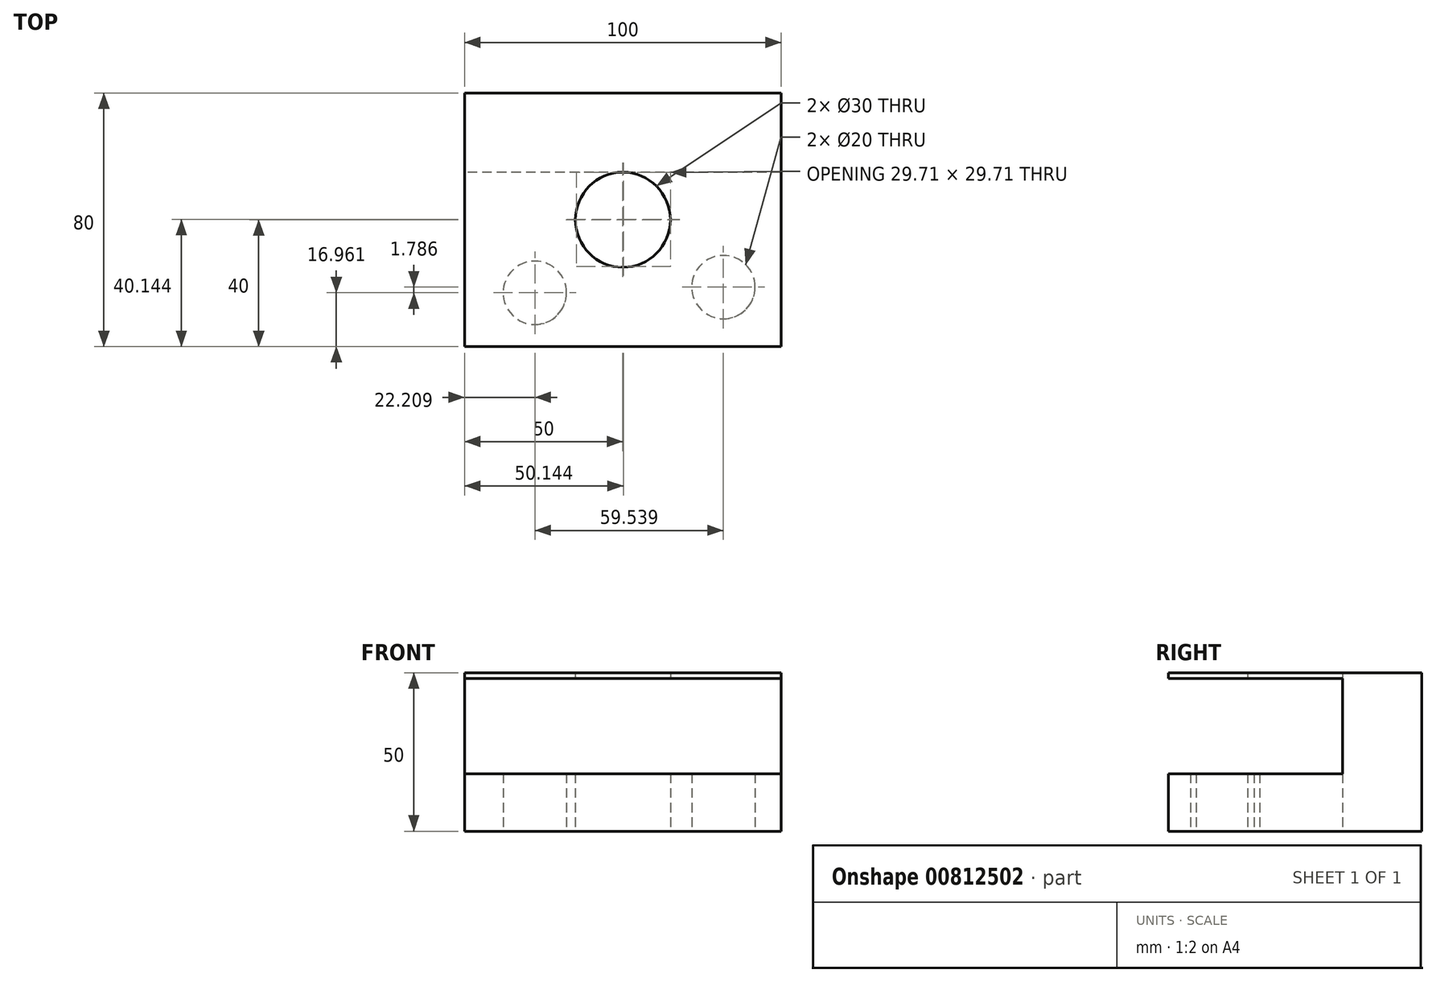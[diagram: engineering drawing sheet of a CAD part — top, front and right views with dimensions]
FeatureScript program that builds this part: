
annotation { "Feature Type Name" : "Feature", "Feature Type Description" : "" }
export const myFeature = defineFeature(function(context is Context, id is Id, definition is map)
    precondition{}
    {
        {
            var Q0;
            Q0=qCreatedBy(makeId("Top.planeOp"),FACE);
            var sketch = newSketch(context, id + "F0", { "sketchPlane" : qUnion([Q0])});
            skLineSegment(sketch, "E0.bottom", {"start": v(-50, 40) * mm, "end": v(50, 40) * mm});
            skLineSegment(sketch, "E0.top", {"start": v(-50, -40) * mm, "end": v(50, -40) * mm});
            skLineSegment(sketch, "E0.left", {"start": v(-50, 40) * mm, "end": v(-50, -40) * mm});
            skLineSegment(sketch, "E0.right", {"start": v(50, 40) * mm, "end": v(50, -40) * mm});
            skCircle(sketch, "E1", {"center": v(0, 0) * mm, "radius": 15 * mm});
            skSolve(sketch);
        }
        {
            var Q0;
            Q0 = qSketchRegion(id + "F0", true);
            extrude(context, id + "F1", {"entities" : qUnion([Q0]), "depth" : 50 * mm, "offsetDistance" : 25 * mm});
        }
        {
            var Q0;
            Q0=qCreatedBy(makeId("Right.planeOp"),FACE);
            var sketch = newSketch(context, id + "F2", { "sketchPlane" : qUnion([Q0])});
            skLineSegment(sketch, "E2.bottom", {"start": v(-85, 48.17) * mm, "end": v(15, 48.17) * mm});
            skLineSegment(sketch, "E2.top", {"start": v(-85, 18.17) * mm, "end": v(15, 18.17) * mm});
            skLineSegment(sketch, "E2.left", {"start": v(-85, 48.17) * mm, "end": v(-85, 18.17) * mm});
            skLineSegment(sketch, "E2.right", {"start": v(15, 48.17) * mm, "end": v(15, 18.17) * mm});
            skSolve(sketch);
        }
        {
            var Q0;
            Q0 = qSketchRegion(id + "F2", true);
            extrude(context, id + "F3", {"entities" : qUnion([Q0]), "operationType" : NewBodyOperationType.REMOVE, "endBound" : BoundingType.THROUGH_ALL, "depth" : 25 * mm, "offsetDistance" : 25 * mm, "hasSecondDirection" : true, "secondDirectionOppositeDirection" : true, "secondDirectionDepth" : 105.8 * mm});
        }
        {
            var Q0;
            Q0=qCreatedBy(makeId("Top.planeOp"),FACE);
            var sketch = newSketch(context, id + "F4", { "sketchPlane" : qUnion([Q0])});
            skCircle(sketch, "E3", {"center": v(-27.8, -23.04) * mm, "radius": 10 * mm});
            skCircle(sketch, "E4", {"center": v(31.75, -21.25) * mm, "radius": 10 * mm});
            skSolve(sketch);
        }
        {
            var Q0;
            Q0 = qSketchRegion(id + "F4", true);
            extrude(context, id + "F5", {"entities" : qUnion([Q0]), "operationType" : NewBodyOperationType.REMOVE, "depth" : 23.4 * mm, "offsetDistance" : 25 * mm});
        }
    });
